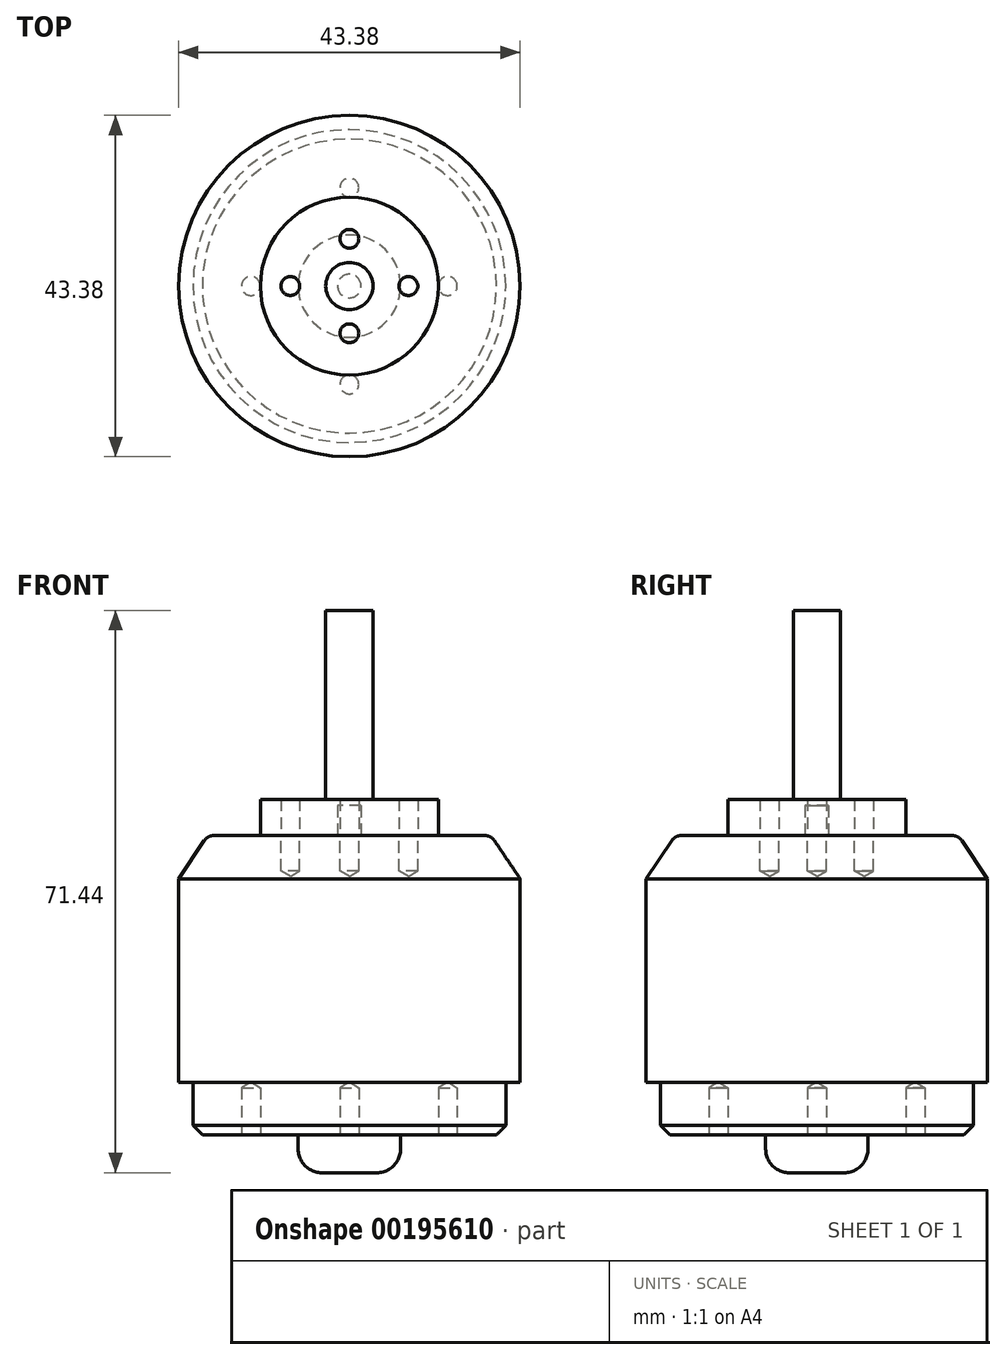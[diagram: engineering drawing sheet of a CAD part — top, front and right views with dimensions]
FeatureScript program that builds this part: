
annotation { "Feature Type Name" : "Feature", "Feature Type Description" : "" }
export const myFeature = defineFeature(function(context is Context, id is Id, definition is map)
    precondition{}
    {
        {
            var Q0;
            Q0=qCreatedBy(makeId("Top.planeOp"),FACE);
            var sketch = newSketch(context, id + "F0", { "sketchPlane" : qUnion([Q0])});
            skCircle(sketch, "E0", {"center": v(0, 0) * mm, "radius": 21.68 * mm});
            skSolve(sketch);
        }
        {
            var Q0;
            Q0 = qSketchRegion(id + "F0", true);
            extrude(context, id + "F1", {"entities" : qUnion([Q0]), "depth" : 31.34 * mm});
        }
        {
            var Q0;
            Q0=qCreatedBy(makeId("Top.planeOp"),FACE);
            var sketch = newSketch(context, id + "F2", { "sketchPlane" : qUnion([Q0])});
            skCircle(sketch, "E1", {"center": v(0, 0) * mm, "radius": 19.88 * mm});
            skSolve(sketch);
        }
        {
            var Q0;
            Q0=makeQuery(id+"F2.imprint","IMPRINT",FACE,{"disambiguationData":[TD([[makeQuery(id+"F2.imprint","IMPRINT",EDGE,{"derivedFrom":sQuery(id+"F2.wireOp",EDGE,"E1")}),1.0]])]});
            extrude(context, id + "F3", {"entities" : qUnion([Q0]), "operationType" : NewBodyOperationType.ADD, "oppositeDirection" : true, "depth" : 6.7 * mm});
        }
        {
            var Q0;
            Q0=makeQuery(id+"F1.opExtrude","CAP_EDGE",EDGE,{"disambiguationData":[OSD([sQuery(id+"F0.wireOp",EDGE,"E0")])],"isStart":false});
            chamfer(context, id + "F4", {"entities" : qUnion([Q0]), "chamferType" : ChamferType.TWO_OFFSETS, "width1" : 3.7 * mm, "oppositeDirection" : false, "width2" : 5.5 * mm, "tangentPropagation" : true});
        }
        {
            var Q0;
            {var subQ0=sQuery(id+"F0.wireOp",EDGE,"E0");Q0=makeQuery(id+"F4.opChamfer","BLEND_EDGE",EDGE,{"blendedFrom":[makeQuery(id+"F1.opExtrude","CAP_EDGE",EDGE,{"disambiguationData":[OSD([subQ0])],"isStart":false}),makeQuery(id+"F1.opExtrude","CAP_FACE",FACE,{"disambiguationData":[OSD([subQ0])],"isStart":false})],"blendedInto":[makeQuery(id+"F1.opExtrude","CAP_FACE",FACE,{"disambiguationData":[OSD([subQ0])],"isStart":false})]});}
            fillet(context, id + "F5", {"entities" : qUnion([Q0]), "radius" : 1.5 * mm, "tangentPropagation" : true, "allowEdgeOverflow" : false});
        }
        {
            var Q0;
            Q0=makeQuery(id+"F3.opExtrude","CAP_EDGE",EDGE,{"disambiguationData":[OSD([sQuery(id+"F2.wireOp",EDGE,"E1")])],"isStart":false});
            chamfer(context, id + "F6", {"entities" : qUnion([Q0]), "width" : 1.2 * mm, "tangentPropagation" : true});
        }
        {
            var Q0;
            Q0=makeQuery(id+"F1.opExtrude","CAP_FACE",FACE,{"disambiguationData":[OSD([sQuery(id+"F0.wireOp",EDGE,"E0")])],"isStart":false});
            var sketch = newSketch(context, id + "F7", { "sketchPlane" : qUnion([Q0])});
            skCircle(sketch, "E2", {"center": v(0, 0) * mm, "radius": 1.5 * mm});
            skSolve(sketch);
        }
        {
            var Q0;
            Q0 = qSketchRegion(id + "F7", true);
            var Q1;
            Q1 = qConstructionFilter(qBodyType(qCreatedBy(id + "F7" ,EDGE), BodyType.WIRE), ConstructionObject.NO);
            extrude(context, id + "F8", {"entities" : qUnion([Q0]), "operationType" : NewBodyOperationType.ADD, "surfaceEntities" : qUnion([Q1]), "depth" : 3.8 * mm});
        }
        {
            var Q0;
            Q0=makeQuery(id+"F3.opExtrude","CAP_FACE",FACE,{"disambiguationData":[OSD([sQuery(id+"F2.wireOp",EDGE,"E1")])],"isStart":false});
            var sketch = newSketch(context, id + "F9", { "sketchPlane" : qUnion([Q0])});
            skPoint(sketch, "E3", {"position": v(-12.5, 0) * mm});
            skPoint(sketch, "E4", {"position": v(12.5, 0) * mm});
            skPoint(sketch, "E5", {"position": v(0, 12.5) * mm});
            skPoint(sketch, "E6", {"position": v(0, -12.5) * mm});
            skSolve(sketch);
        }
        {
            var Q0;
            Q0=sQuery(id+"F9.wireOp",VERTEX,"E5");
            var Q1;
            Q1=sQuery(id+"F9.wireOp",VERTEX,"E3");
            var Q2;
            Q2=sQuery(id+"F9.wireOp",VERTEX,"E6");
            var Q3;
            Q3=sQuery(id+"F9.wireOp",VERTEX,"E4");
            var Q4;
            Q4=makeQuery(id+"F1.opExtrude","SWEPT_BODY",BODY,{"disambiguationData":[OSD([sQuery(id+"F0.wireOp",EDGE,"E0")])]});
            hole(context, id + "F10", {"style" : HoleStyle.SIMPLE, "endStyle" : HoleEndStyle.BLIND, "standardTappedOrClearance" : lookupTablePath({ "standard" : "ISO", "engagement" : "75%", "pitch" : "0.6 mm", "size" : "M3", "type" : "Tapped" }), "standardBlindInLast" : lookupTablePath({ "standard" : "ISO", "engagement" : "75%", "pitch" : "0.6 mm", "size" : "M3", "type" : "Tapped" }), "holeDiameter" : 2.4 * mm, "holeDepth" : 6 * mm, "locations" : qUnion([Q0, Q1, Q2, Q3]), "scope" : qUnion([Q4])});
        }
        {
            var Q0;
            Q0=makeQuery(id+"F3.opExtrude","CAP_FACE",FACE,{"disambiguationData":[OSD([sQuery(id+"F2.wireOp",EDGE,"E1")])],"isStart":false});
            var sketch = newSketch(context, id + "F11", { "sketchPlane" : qUnion([Q0])});
            skCircle(sketch, "E7", {"center": v(0, 0) * mm, "radius": 6.5 * mm});
            skSolve(sketch);
        }
        {
            var Q0;
            Q0 = qSketchRegion(id + "F11", true);
            extrude(context, id + "F12", {"entities" : qUnion([Q0]), "operationType" : NewBodyOperationType.ADD, "depth" : 4.8 * mm});
        }
        {
            var Q0;
            Q0=makeQuery(id+"F12.opExtrude","CAP_EDGE",EDGE,{"disambiguationData":[OSD([sQuery(id+"F11.wireOp",EDGE,"E7")])],"isStart":false});
            fillet(context, id + "F13", {"entities" : qUnion([Q0]), "radius" : 3 * mm, "tangentPropagation" : true, "allowEdgeOverflow" : false});
        }
        {
            var Q0;
            Q0=makeQuery(id+"F1.opExtrude","CAP_FACE",FACE,{"disambiguationData":[OSD([sQuery(id+"F0.wireOp",EDGE,"E0")])],"isStart":false});
            var sketch = newSketch(context, id + "F14", { "sketchPlane" : qUnion([Q0])});
            skPoint(sketch, "E8", {"position": v(-7.5, 0) * mm});
            skPoint(sketch, "E9", {"position": v(7.5, 0) * mm});
            skPoint(sketch, "E10", {"position": v(0, 6) * mm});
            skPoint(sketch, "E11", {"position": v(0, -6) * mm});
            skSolve(sketch);
        }
        {
            var Q0;
            Q0=sQuery(id+"F14.wireOp",VERTEX,"E11");
            var Q1;
            Q1=sQuery(id+"F14.wireOp",VERTEX,"E10");
            var Q2;
            Q2=sQuery(id+"F14.wireOp",VERTEX,"E9");
            var Q3;
            Q3=sQuery(id+"F14.wireOp",VERTEX,"E8");
            var Q4;
            Q4=makeQuery(id+"F1.opExtrude","SWEPT_BODY",BODY,{"disambiguationData":[OSD([sQuery(id+"F0.wireOp",EDGE,"E0")])]});
            hole(context, id + "F15", {"style" : HoleStyle.SIMPLE, "endStyle" : HoleEndStyle.BLIND, "standardTappedOrClearance" : lookupTablePath({ "standard" : "ISO", "engagement" : "75%", "pitch" : "0.6 mm", "size" : "M3", "type" : "Tapped" }), "standardBlindInLast" : lookupTablePath({ "standard" : "ISO", "engagement" : "75%", "pitch" : "0.6 mm", "size" : "M3", "type" : "Tapped" }), "holeDiameter" : 2.4 * mm, "holeDepth" : 4.5 * mm, "locations" : qUnion([Q0, Q1, Q2, Q3]), "scope" : qUnion([Q4])});
        }
        {
            var Q0;
            Q0=makeQuery(id+"F1.opExtrude","CAP_FACE",FACE,{"disambiguationData":[OSD([sQuery(id+"F0.wireOp",EDGE,"E0")])],"isStart":false});
            var sketch = newSketch(context, id + "F16", { "sketchPlane" : qUnion([Q0])});
            skCircle(sketch, "E12", {"center": v(0, 0) * mm, "radius": 11.3 * mm});
            skSolve(sketch);
        }
        {
            var Q0;
            Q0 = qSketchRegion(id + "F16", true);
            extrude(context, id + "F17", {"entities" : qUnion([Q0]), "depth" : 4.6 * mm});
        }
        {
            var Q0;
            Q0=sQuery(id+"F14.wireOp",VERTEX,"E11");
            var Q1;
            Q1=sQuery(id+"F14.wireOp",VERTEX,"E8");
            var Q2;
            Q2=sQuery(id+"F14.wireOp",VERTEX,"E9");
            var Q3;
            Q3=sQuery(id+"F14.wireOp",VERTEX,"E10");
            var Q4;
            Q4=makeQuery(id+"F17.opExtrude","SWEPT_BODY",BODY,{"disambiguationData":[OSD([sQuery(id+"F16.wireOp",EDGE,"E12")])]});
            hole(context, id + "F18", {"style" : HoleStyle.SIMPLE, "endStyle" : HoleEndStyle.THROUGH, "oppositeDirection" : true, "standardTappedOrClearance" : lookupTablePath({ "standard" : "ISO", "engagement" : "75%", "pitch" : "0.6 mm", "size" : "M3", "type" : "Tapped" }), "standardBlindInLast" : lookupTablePath({ "standard" : "ISO", "engagement" : "75%", "pitch" : "0.6 mm", "size" : "M3", "type" : "Tapped" }), "holeDiameter" : 2.4 * mm, "locations" : qUnion([Q0, Q1, Q2, Q3]), "scope" : qUnion([Q4]), "isTappedThrough" : true, "showTappedDepth" : true});
        }
        {
            var Q0;
            Q0=makeQuery(id+"F17.opExtrude","CAP_FACE",FACE,{"disambiguationData":[OSD([sQuery(id+"F16.wireOp",EDGE,"E12")])],"isStart":false});
            var sketch = newSketch(context, id + "F19", { "sketchPlane" : qUnion([Q0])});
            skCircle(sketch, "E13", {"center": v(0, 0) * mm, "radius": 3 * mm});
            skSolve(sketch);
        }
        {
            var Q0;
            Q0 = qSketchRegion(id + "F19", true);
            extrude(context, id + "F20", {"entities" : qUnion([Q0]), "operationType" : NewBodyOperationType.ADD, "depth" : 24 * mm});
        }
    });
